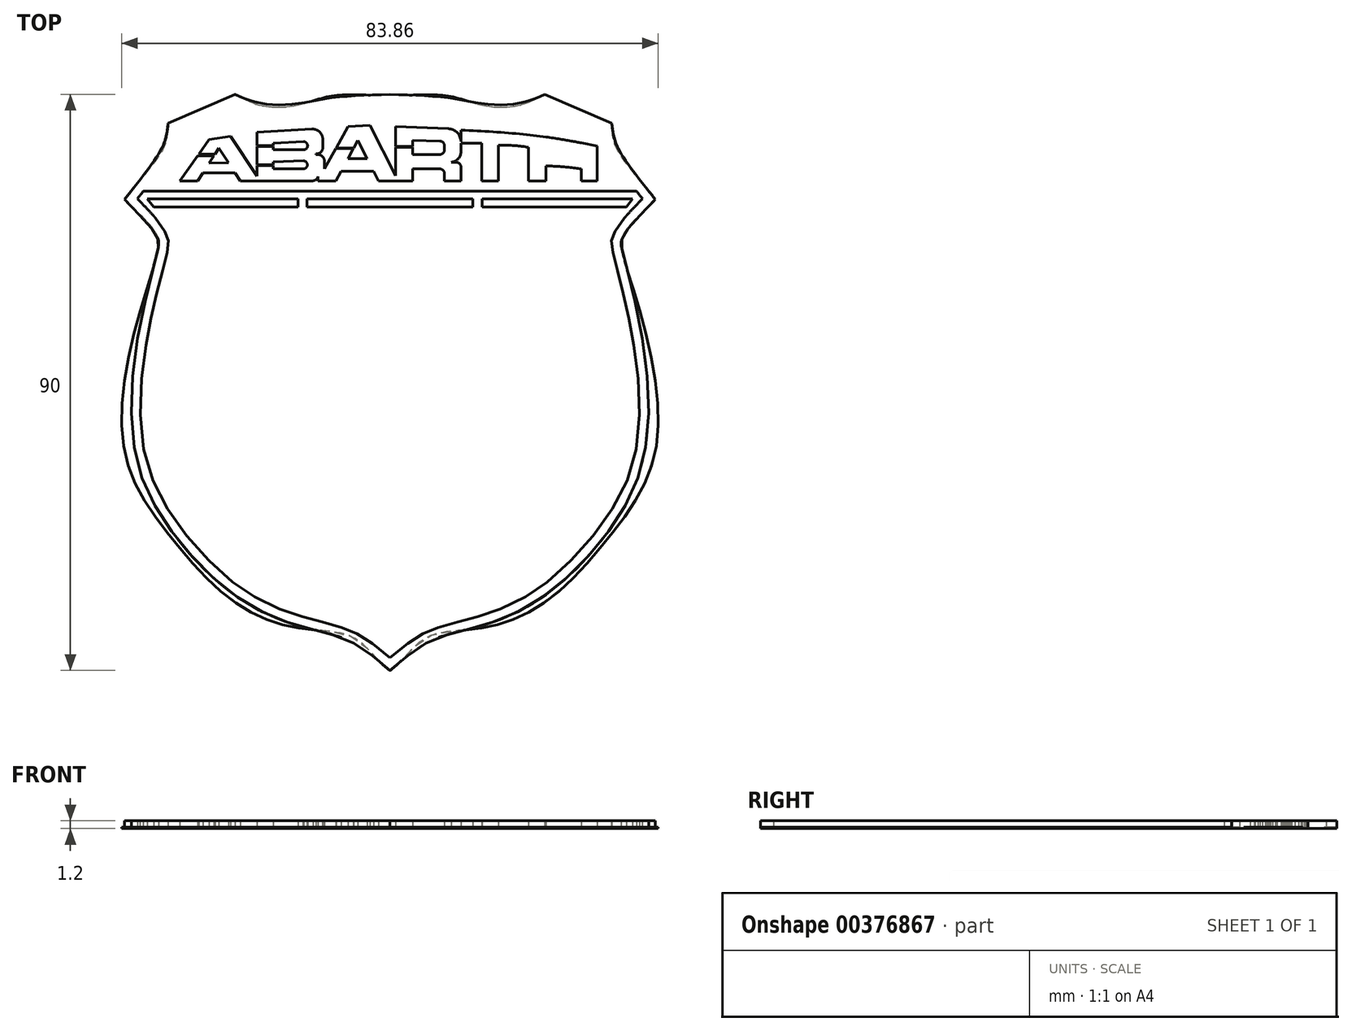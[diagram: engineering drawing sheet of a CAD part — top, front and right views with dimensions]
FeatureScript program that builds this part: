
annotation { "Feature Type Name" : "Feature", "Feature Type Description" : "" }
export const myFeature = defineFeature(function(context is Context, id is Id, definition is map)
    precondition{}
    {
        {
            var Q0;
            Q0=qCreatedBy(makeId("Top.planeOp"),FACE);
            var sketch = newSketch(context, id + "F0", { "sketchPlane" : qUnion([Q0])});
            skFitSpline(sketch, "E0", {"points": [v(-41.47, 27.67) * mm, v(-37.34, 23.25) * mm, v(-36.2, 21.38) * mm, v(-36.2, 20.2) * mm, v(-39.18, 7.45) * mm, v(-39.76, -12.14) * mm, v(-33.8, -24.6) * mm, v(-23.5, -34.67) * mm, v(-13.75, -39.08) * mm, v(-6.19, -41.36) * mm, v(0, -45.92) * mm], "startDerivative": vector(56.35, -56.79) * mm, "endDerivative": vector(62.68, -55.45) * mm});
            skFitSpline(sketch, "E1", {"points": [v(-41.47, 27.67) * mm, v(-36.79, 33.8) * mm, v(-35.15, 36.9) * mm, v(-34.66, 39.57) * mm], "startDerivative": vector(11.93, 14.97) * mm, "endDerivative": vector(1.2, 10.34) * mm});
            skLineSegment(sketch, "E2", {"start": v(-34.66, 39.57) * mm, "end": v(-24.2, 44.08) * mm});
            skFitSpline(sketch, "E3", {"points": [v(-24.2, 44.08) * mm, v(-20.64, 42.8) * mm, v(-15.26, 42.56) * mm, v(-9.28, 43.52) * mm, v(0, 44.08) * mm], "startDerivative": vector(16.73, -7.4) * mm, "endDerivative": vector(31.53, 0.89) * mm});
            skFitSpline(sketch, "E4.0", {"points": [v(-40.4, 28.73) * mm, v(-39.82, 28.14) * mm, v(-38.93, 27.25) * mm, v(-37.83, 26.1) * mm, v(-37.06, 25.25) * mm, v(-36.37, 24.45) * mm, v(-35.77, 23.67) * mm, v(-35.37, 23.07) * mm, v(-35.1, 22.6) * mm, v(-34.93, 22.26) * mm, v(-34.81, 21.96) * mm, v(-34.74, 21.72) * mm, v(-34.66, 21.45) * mm, v(-34.61, 21.08) * mm, v(-34.62, 20.65) * mm, v(-34.66, 20.25) * mm, v(-34.74, 19.86) * mm, v(-34.83, 19.41) * mm, v(-35, 18.73) * mm, v(-35.25, 17.72) * mm, v(-35.62, 16.26) * mm, v(-36.04, 14.6) * mm, v(-36.5, 12.79) * mm, v(-36.95, 10.84) * mm, v(-37.39, 8.81) * mm, v(-37.8, 6.74) * mm, v(-38.26, 3.96) * mm, v(-38.7, 0.48) * mm, v(-38.96, -3.62) * mm, v(-38.9, -7.54) * mm, v(-38.49, -11.2) * mm, v(-37.69, -14.47) * mm, v(-36.5, -17.48) * mm, v(-34.99, -20.3) * mm, v(-33.15, -23.03) * mm, v(-31.03, -25.73) * mm, v(-28.7, -28.33) * mm, v(-26.22, -30.71) * mm, v(-24.07, -32.46) * mm, v(-22.34, -33.66) * mm, v(-20.6, -34.74) * mm, v(-18.4, -35.86) * mm, v(-16.2, -36.74) * mm, v(-14.45, -37.31) * mm, v(-13.16, -37.69) * mm, v(-11.88, -38.02) * mm, v(-10.6, -38.34) * mm, v(-9.3, -38.66) * mm, v(-8.03, -39.03) * mm, v(-6.97, -39.4) * mm, v(-6.12, -39.73) * mm, v(-5.5, -40.02) * mm, v(-4.88, -40.34) * mm, v(-4.09, -40.79) * mm, v(-3.14, -41.4) * mm, v(-2.05, -42.21) * mm, v(-0.65, -43.34) * mm, v(0.34, -44.22) * mm, v(1, -44.8) * mm]});
            skFitSpline(sketch, "E5.0", {"points": [v(-40.3, 26.74) * mm, v(-39.8, 27.36) * mm, v(-38.8, 28.61) * mm, v(-37.38, 30.44) * mm, v(-36.31, 31.86) * mm, v(-35.57, 32.92) * mm, v(-34.9, 33.92) * mm, v(-34.35, 34.87) * mm, v(-33.97, 35.72) * mm, v(-33.79, 36.21) * mm, v(-33.63, 36.71) * mm, v(-33.47, 37.33) * mm, v(-33.3, 38.29) * mm, v(-33.22, 38.97) * mm, v(-33.17, 39.4) * mm]});
            skLineSegment(sketch, "E6", {"start": v(-38.54, 28.95) * mm, "end": v(0, 28.95) * mm});
            skLineSegment(sketch, "E7", {"start": v(-37.07, 25.26) * mm, "end": v(0, 25.26) * mm});
            skLineSegment(sketch, "E8", {"start": v(-37.9, 27.74) * mm, "end": v(-14.38, 27.74) * mm});
            skLineSegment(sketch, "E9", {"start": v(-36.92, 26.5) * mm, "end": v(-14.38, 26.5) * mm});
            skLineSegment(sketch, "E10", {"start": v(-14.38, 27.74) * mm, "end": v(-14.38, 26.5) * mm});
            skLineSegment(sketch, "E11", {"start": v(-37.9, 27.74) * mm, "end": v(-36.92, 26.5) * mm});
            skLineSegment(sketch, "E12", {"start": v(-12.98, 27.74) * mm, "end": v(0, 27.74) * mm});
            skLineSegment(sketch, "E13", {"start": v(-12.98, 26.5) * mm, "end": v(0, 26.5) * mm});
            skLineSegment(sketch, "E14", {"start": v(-12.98, 27.74) * mm, "end": v(-12.98, 26.5) * mm});
            skPoint(sketch, "E15.orphan", {"position": v(-13.21, 26.5) * mm});
            skLineSegment(sketch, "E16", {"start": v(-36.64, 24.77) * mm, "end": v(0, 24.77) * mm});
            skFitSpline(sketch, "E17.trimOffspring", {"points": [v(-40.4, 28.73) * mm, v(-39.82, 28.14) * mm, v(-38.93, 27.25) * mm, v(-37.83, 26.1) * mm, v(-37.06, 25.25) * mm, v(-36.37, 24.45) * mm, v(-35.77, 23.67) * mm, v(-35.37, 23.07) * mm, v(-35.1, 22.6) * mm, v(-34.93, 22.26) * mm, v(-34.81, 21.96) * mm, v(-34.74, 21.72) * mm, v(-34.66, 21.45) * mm, v(-34.61, 21.08) * mm, v(-34.62, 20.65) * mm, v(-34.66, 20.25) * mm, v(-34.74, 19.86) * mm, v(-34.83, 19.41) * mm, v(-35, 18.73) * mm, v(-35.25, 17.72) * mm, v(-35.62, 16.26) * mm, v(-36.04, 14.6) * mm, v(-36.5, 12.79) * mm, v(-36.95, 10.84) * mm, v(-37.39, 8.81) * mm, v(-37.8, 6.74) * mm, v(-38.26, 3.96) * mm, v(-38.7, 0.48) * mm, v(-38.96, -3.62) * mm, v(-38.9, -7.54) * mm, v(-38.49, -11.2) * mm, v(-37.69, -14.47) * mm, v(-36.5, -17.48) * mm, v(-34.99, -20.3) * mm, v(-33.15, -23.03) * mm, v(-31.03, -25.73) * mm, v(-28.7, -28.33) * mm, v(-26.22, -30.71) * mm, v(-24.07, -32.46) * mm, v(-22.34, -33.66) * mm, v(-20.6, -34.74) * mm, v(-18.4, -35.86) * mm, v(-16.2, -36.74) * mm, v(-14.45, -37.31) * mm, v(-13.16, -37.69) * mm, v(-11.88, -38.02) * mm, v(-10.6, -38.34) * mm, v(-9.3, -38.66) * mm, v(-8.03, -39.03) * mm, v(-6.97, -39.4) * mm, v(-6.12, -39.73) * mm, v(-5.5, -40.02) * mm, v(-4.88, -40.34) * mm, v(-4.09, -40.79) * mm, v(-3.14, -41.4) * mm, v(-2.05, -42.21) * mm, v(-0.65, -43.34) * mm, v(0.34, -44.22) * mm, v(1, -44.8) * mm]});
            skLineSegment(sketch, "E18.MirrorCS", {"start": v(37.9, 27.74) * mm, "end": v(36.92, 26.5) * mm});
            skLineSegment(sketch, "E19.MirrorCS", {"start": v(14.38, 27.74) * mm, "end": v(14.38, 26.5) * mm});
            skLineSegment(sketch, "E20.MirrorCS", {"start": v(12.98, 27.74) * mm, "end": v(12.98, 26.5) * mm});
            skFitSpline(sketch, "E21.MirrorCS", {"points": [v(41.47, 27.67) * mm, v(36.79, 33.8) * mm, v(35.15, 36.9) * mm, v(34.66, 39.57) * mm], "startDerivative": vector(-11.93, 14.97) * mm, "endDerivative": vector(-1.2, 10.34) * mm});
            skLineSegment(sketch, "E22.MirrorCS", {"start": v(12.98, 26.5) * mm, "end": v(0, 26.5) * mm});
            skLineSegment(sketch, "E23.MirrorCS", {"start": v(37.9, 27.74) * mm, "end": v(14.38, 27.74) * mm});
            skLineSegment(sketch, "E24.MirrorCS", {"start": v(34.66, 39.57) * mm, "end": v(24.2, 44.08) * mm});
            skLineSegment(sketch, "E25.MirrorCS", {"start": v(37.07, 25.26) * mm, "end": v(0, 25.26) * mm});
            skFitSpline(sketch, "E26.MirrorCS", {"points": [v(24.2, 44.08) * mm, v(20.64, 42.8) * mm, v(15.26, 42.56) * mm, v(9.28, 43.52) * mm, v(0, 44.08) * mm], "startDerivative": vector(-16.73, -7.4) * mm, "endDerivative": vector(-31.53, 0.89) * mm});
            skLineSegment(sketch, "E27.MirrorCS", {"start": v(12.98, 27.74) * mm, "end": v(0, 27.74) * mm});
            skLineSegment(sketch, "E28.MirrorCS", {"start": v(36.64, 24.77) * mm, "end": v(0, 24.77) * mm});
            skLineSegment(sketch, "E29.MirrorCS", {"start": v(36.92, 26.5) * mm, "end": v(14.38, 26.5) * mm});
            skPoint(sketch, "E30.MirrorP", {"position": v(13.21, 26.5) * mm});
            skLineSegment(sketch, "E31.MirrorCS", {"start": v(38.54, 28.95) * mm, "end": v(0, 28.95) * mm});
            skFitSpline(sketch, "E32.MirrorCS", {"points": [v(41.47, 27.67) * mm, v(37.34, 23.25) * mm, v(36.2, 21.38) * mm, v(36.2, 20.2) * mm, v(39.18, 7.45) * mm, v(39.76, -12.14) * mm, v(33.8, -24.6) * mm, v(23.5, -34.67) * mm, v(13.75, -39.08) * mm, v(6.19, -41.36) * mm, v(0, -45.92) * mm], "startDerivative": vector(-56.35, -56.79) * mm, "endDerivative": vector(-62.68, -55.45) * mm});
            skLineSegment(sketch, "E33", {"start": v(-32.83, 30.58) * mm, "end": v(-30.04, 34.53) * mm});
            skLineSegment(sketch, "E34", {"start": v(-28.26, 37.05) * mm, "end": v(-24.93, 37.53) * mm});
            skLineSegment(sketch, "E35", {"start": v(-24.93, 37.53) * mm, "end": v(-20.8, 31.35) * mm});
            skLineSegment(sketch, "E36", {"start": v(-20.8, 31.35) * mm, "end": v(-20.8, 32.99) * mm});
            skLineSegment(sketch, "E37", {"start": v(-20.8, 38.16) * mm, "end": v(-12.23, 38.67) * mm});
            skLineSegment(sketch, "E38", {"start": v(-32.83, 30.58) * mm, "end": v(-30.05, 30.58) * mm});
            skLineSegment(sketch, "E39", {"start": v(-30.05, 30.58) * mm, "end": v(-29.25, 31.8) * mm});
            skLineSegment(sketch, "E40", {"start": v(-26.72, 35.7) * mm, "end": v(-25.24, 33.42) * mm});
            skLineSegment(sketch, "E41", {"start": v(-29.25, 31.8) * mm, "end": v(-24.2, 31.8) * mm});
            skLineSegment(sketch, "E42", {"start": v(-25.24, 33.42) * mm, "end": v(-28.24, 33.35) * mm});
            skLineSegment(sketch, "E43.trimOffspring", {"start": v(-28.24, 33.35) * mm, "end": v(-27.48, 34.53) * mm});
            skLineSegment(sketch, "E44.trimOffspring", {"start": v(-24.2, 31.8) * mm, "end": v(-23.4, 30.58) * mm});
            skLineSegment(sketch, "E45.trimOffspring", {"start": v(-23.4, 30.58) * mm, "end": v(-11.99, 30.58) * mm});
            skLineSegment(sketch, "E46", {"start": v(-6.54, 39.04) * mm, "end": v(-3.12, 39.25) * mm});
            skLineSegment(sketch, "E47", {"start": v(-3.12, 39.25) * mm, "end": v(0.88, 31.36) * mm});
            skLineSegment(sketch, "E48", {"start": v(0.88, 31.36) * mm, "end": v(0.88, 35.83) * mm});
            skLineSegment(sketch, "E49", {"start": v(0.88, 39.04) * mm, "end": v(9.14, 38.73) * mm});
            skLineSegment(sketch, "E50", {"start": v(11.09, 36.44) * mm, "end": v(14.35, 36.44) * mm});
            skLineSegment(sketch, "E51", {"start": v(14.35, 36.44) * mm, "end": v(14.35, 30.58) * mm});
            skLineSegment(sketch, "E52", {"start": v(16.96, 36.17) * mm, "end": v(16.96, 30.58) * mm});
            skLineSegment(sketch, "E53", {"start": v(3.52, 36.9) * mm, "end": v(3.52, 35.93) * mm});
            skLineSegment(sketch, "E54", {"start": v(8.52, 36.06) * mm, "end": v(8.52, 35.45) * mm});
            skLineSegment(sketch, "E55", {"start": v(3.52, 36.9) * mm, "end": v(7.78, 36.81) * mm});
            skLineSegment(sketch, "E56", {"start": v(3.52, 34.7) * mm, "end": v(7.77, 34.7) * mm});
            skPoint(sketch, "E57.orphan", {"position": v(8.52, 36.97) * mm});
            skLineSegment(sketch, "E58", {"start": v(3.52, 32.45) * mm, "end": v(7.77, 32.45) * mm});
            skLineSegment(sketch, "E59", {"start": v(8.52, 31.7) * mm, "end": v(8.52, 30.58) * mm});
            skLineSegment(sketch, "E60", {"start": v(11.09, 32.75) * mm, "end": v(11.09, 30.58) * mm});
            skLineSegment(sketch, "E61", {"start": v(11.09, 36.7) * mm, "end": v(11.09, 38.49) * mm});
            skLineSegment(sketch, "E62", {"start": v(9.6, 33.5) * mm, "end": v(10.34, 33.5) * mm});
            skLineSegment(sketch, "E63.trimOffspring", {"start": v(3.52, 32.45) * mm, "end": v(3.52, 30.58) * mm});
            skPoint(sketch, "E64.visualSharp", {"position": v(8.52, 36.8) * mm});
            skArc(sketch, "E64.filletArc", {"start": v(8.52, 36.06) * mm, "mid": v(8.3, 36.59) * mm, "end": v(7.78, 36.81) * mm});
            skPoint(sketch, "E65.visualSharp", {"position": v(8.52, 34.7) * mm});
            skArc(sketch, "E65.filletArc", {"start": v(7.77, 34.7) * mm, "mid": v(8.3, 34.91) * mm, "end": v(8.52, 35.45) * mm});
            skArc(sketch, "E66.filletArc", {"start": v(8.52, 31.7) * mm, "mid": v(8.3, 32.23) * mm, "end": v(7.77, 32.45) * mm});
            skPoint(sketch, "E67.visualSharp", {"position": v(11.09, 33.5) * mm});
            skArc(sketch, "E67.filletArc", {"start": v(11.09, 32.75) * mm, "mid": v(10.87, 33.28) * mm, "end": v(10.34, 33.5) * mm});
            skLineSegment(sketch, "E68", {"start": v(-8.43, 30.58) * mm, "end": v(-7.62, 32.1) * mm});
            skLineSegment(sketch, "E69", {"start": v(-5.03, 36.94) * mm, "end": v(-3.54, 34.04) * mm});
            skLineSegment(sketch, "E70", {"start": v(-7.62, 32.1) * mm, "end": v(-2.54, 32.1) * mm});
            skLineSegment(sketch, "E71", {"start": v(-6.58, 34.04) * mm, "end": v(-3.54, 34.04) * mm});
            skLineSegment(sketch, "E72.trimOffspring", {"start": v(-6.58, 34.04) * mm, "end": v(-5.73, 35.62) * mm});
            skLineSegment(sketch, "E73.trimOffspring", {"start": v(-2.54, 32.1) * mm, "end": v(-1.76, 30.58) * mm});
            skLineSegment(sketch, "E74.trimOffspring", {"start": v(-1.76, 30.58) * mm, "end": v(3.52, 30.58) * mm});
            skLineSegment(sketch, "E75.trimOffspring", {"start": v(8.52, 30.58) * mm, "end": v(11.09, 30.58) * mm});
            skLineSegment(sketch, "E76", {"start": v(21.66, 35.8) * mm, "end": v(21.66, 30.58) * mm});
            skLineSegment(sketch, "E77", {"start": v(24.37, 32.92) * mm, "end": v(24.37, 30.58) * mm});
            skLineSegment(sketch, "E78", {"start": v(29.9, 32.46) * mm, "end": v(29.9, 30.58) * mm});
            skLineSegment(sketch, "E79", {"start": v(24.37, 34.71) * mm, "end": v(24.37, 37.44) * mm});
            skLineSegment(sketch, "E80", {"start": v(29.9, 34.15) * mm, "end": v(29.9, 36.5) * mm});
            skFitSpline(sketch, "E81", {"points": [v(24.37, 34.71) * mm, v(27.2, 34.5) * mm, v(29.9, 34.15) * mm], "startDerivative": vector(5.62, -0.36) * mm, "endDerivative": vector(5.44, -0.76) * mm});
            skFitSpline(sketch, "E82", {"points": [v(24.37, 32.92) * mm, v(27.07, 32.78) * mm, v(29.9, 32.46) * mm], "startDerivative": vector(5.44, -0.19) * mm, "endDerivative": vector(5.62, -0.73) * mm});
            skLineSegment(sketch, "E83", {"start": v(32.4, 36.02) * mm, "end": v(32.4, 30.58) * mm});
            skFitSpline(sketch, "E84", {"points": [v(32.4, 36.02) * mm, v(29.9, 36.5) * mm, v(24.37, 37.44) * mm, v(11.09, 38.49) * mm], "startDerivative": vector(-11.08, 2.13) * mm, "endDerivative": vector(-30.4, 0.87) * mm});
            skFitSpline(sketch, "E85", {"points": [v(16.96, 36.17) * mm, v(19.52, 36.08) * mm, v(21.66, 35.8) * mm], "startDerivative": vector(5.24, 0.1) * mm, "endDerivative": vector(6.05, -1.14) * mm});
            skLineSegment(sketch, "E86.trimOffspring", {"start": v(29.9, 30.58) * mm, "end": v(32.4, 30.58) * mm});
            skLineSegment(sketch, "E87.trimOffspring", {"start": v(21.66, 30.58) * mm, "end": v(24.37, 30.58) * mm});
            skLineSegment(sketch, "E88.trimOffspring", {"start": v(14.35, 30.58) * mm, "end": v(16.96, 30.58) * mm});
            skLineSegment(sketch, "E89", {"start": v(-18.2, 36.49) * mm, "end": v(-18.2, 36.06) * mm});
            skLineSegment(sketch, "E90", {"start": v(-18.2, 32.46) * mm, "end": v(-13.58, 32.46) * mm});
            skLineSegment(sketch, "E91", {"start": v(-18.2, 33.52) * mm, "end": v(-13.5, 33.72) * mm});
            skLineSegment(sketch, "E92", {"start": v(-18.2, 35.43) * mm, "end": v(-13.54, 35.43) * mm});
            skLineSegment(sketch, "E93", {"start": v(-18.2, 36.49) * mm, "end": v(-13.47, 36.7) * mm});
            skLineSegment(sketch, "E94", {"start": v(-13.47, 36.7) * mm, "end": v(-13.54, 35.43) * mm, "construction": true});
            skLineSegment(sketch, "E95", {"start": v(-13.5, 33.72) * mm, "end": v(-13.58, 32.46) * mm, "construction": true});
            skLineSegment(sketch, "E96.trimOffspring", {"start": v(-18.2, 33.52) * mm, "end": v(-18.2, 33.09) * mm});
            skArc(sketch, "E97", {"start": v(-13.54, 35.43) * mm, "mid": v(-12.86, 36.1) * mm, "end": v(-13.6, 36.7) * mm});
            skArc(sketch, "E98", {"start": v(-13.58, 32.46) * mm, "mid": v(-12.9, 33.11) * mm, "end": v(-13.63, 33.71) * mm});
            skLineSegment(sketch, "E99", {"start": v(-10.5, 37.04) * mm, "end": v(-10.5, 35.92) * mm});
            skLineSegment(sketch, "E100", {"start": v(-10.26, 33.76) * mm, "end": v(-10.26, 32.46) * mm});
            skLineSegment(sketch, "E101.trimOffspring", {"start": v(-11.25, 30.58) * mm, "end": v(-8.43, 30.58) * mm});
            skLineSegment(sketch, "E102.trimOffspring", {"start": v(-10.26, 32.46) * mm, "end": v(-8.47, 35.62) * mm});
            skLineSegment(sketch, "E103", {"start": v(-11.25, 31.24) * mm, "end": v(-11.25, 30.58) * mm});
            skFitSpline(sketch, "E104", {"points": [v(-11.99, 30.58) * mm, v(-11.5, 30.8) * mm, v(-11.25, 31.24) * mm], "startDerivative": vector(1.07, 0.32) * mm, "endDerivative": vector(0.41, 0.99) * mm});
            skLineSegment(sketch, "E105", {"start": v(-11.54, 34.66) * mm, "end": v(-11.16, 34.66) * mm});
            skArc(sketch, "E106.filletArc", {"start": v(-10.26, 33.76) * mm, "mid": v(-10.52, 34.4) * mm, "end": v(-11.16, 34.66) * mm});
            skLineSegment(sketch, "E107", {"start": v(-11.54, 34.66) * mm, "end": v(-11.54, 34.79) * mm});
            skFitSpline(sketch, "E108", {"points": [v(-11.54, 34.79) * mm, v(-10.9, 34.98) * mm, v(-10.51, 35.57) * mm, v(-10.5, 35.92) * mm], "startDerivative": vector(1.88, 0.23) * mm, "endDerivative": vector(0.1, 1.77) * mm});
            skArc(sketch, "E109", {"start": v(-10.5, 37.04) * mm, "mid": v(-11, 38.23) * mm, "end": v(-12.23, 38.67) * mm});
            skPoint(sketch, "E109.first.point", {"position": v(-12.23, 38.67) * mm});
            skPoint(sketch, "E109.second.point", {"position": v(-10.5, 37.04) * mm});
            skPoint(sketch, "E109.third.point", {"position": v(-13.76, 37.07) * mm});
            skPoint(sketch, "E110.second.point", {"position": v(11.09, 36.7) * mm});
            skPoint(sketch, "E110.third.point", {"position": v(7.3, 35.72) * mm});
            skArc(sketch, "E111.trimOffspring", {"start": v(11.09, 36.7) * mm, "mid": v(10.52, 38.1) * mm, "end": v(9.14, 38.73) * mm});
            skLineSegment(sketch, "E112", {"start": v(11.09, 36.44) * mm, "end": v(11.09, 35.12) * mm});
            skPoint(sketch, "E113.second.point", {"position": v(11.09, 35.12) * mm});
            skPoint(sketch, "E113.third.point", {"position": v(10.14, 36.6) * mm});
            skArc(sketch, "E114.trimOffspring", {"start": v(9.6, 33.5) * mm, "mid": v(10.66, 34.02) * mm, "end": v(11.09, 35.12) * mm});
            skLineSegment(sketch, "E115", {"start": v(-35.21, -19.82) * mm, "end": v(-22.8, -14.18) * mm});
            skLineSegment(sketch, "E116", {"start": v(-34.28, -21.33) * mm, "end": v(-5.34, -8.17) * mm});
            skFitSpline(sketch, "E117.0", {"points": [v(40.4, 28.73) * mm, v(39.82, 28.14) * mm, v(38.93, 27.25) * mm, v(37.83, 26.1) * mm, v(37.06, 25.25) * mm, v(36.37, 24.45) * mm, v(35.77, 23.67) * mm, v(35.37, 23.07) * mm, v(35.1, 22.6) * mm, v(34.93, 22.26) * mm, v(34.81, 21.96) * mm, v(34.74, 21.72) * mm, v(34.66, 21.45) * mm, v(34.61, 21.08) * mm, v(34.62, 20.65) * mm, v(34.66, 20.25) * mm, v(34.74, 19.86) * mm, v(34.83, 19.41) * mm, v(35, 18.73) * mm, v(35.25, 17.72) * mm, v(35.62, 16.26) * mm, v(36.04, 14.6) * mm, v(36.5, 12.79) * mm, v(36.95, 10.84) * mm, v(37.39, 8.81) * mm, v(37.8, 6.74) * mm, v(38.26, 3.96) * mm, v(38.7, 0.48) * mm, v(38.96, -3.62) * mm, v(38.9, -7.54) * mm, v(38.49, -11.2) * mm, v(37.69, -14.47) * mm, v(36.5, -17.48) * mm, v(34.99, -20.3) * mm, v(33.15, -23.03) * mm, v(31.03, -25.73) * mm, v(28.7, -28.33) * mm, v(26.22, -30.71) * mm, v(24.07, -32.46) * mm, v(22.34, -33.66) * mm, v(20.6, -34.74) * mm, v(18.4, -35.86) * mm, v(16.2, -36.74) * mm, v(14.45, -37.31) * mm, v(13.16, -37.69) * mm, v(11.88, -38.02) * mm, v(10.6, -38.34) * mm, v(9.3, -38.66) * mm, v(8.03, -39.03) * mm, v(6.97, -39.4) * mm, v(6.12, -39.73) * mm, v(5.5, -40.02) * mm, v(4.88, -40.34) * mm, v(4.09, -40.79) * mm, v(3.14, -41.4) * mm, v(2.05, -42.21) * mm, v(0.65, -43.34) * mm, v(-0.34, -44.22) * mm, v(-1, -44.8) * mm]});
            skFitSpline(sketch, "E118.0", {"points": [v(40.3, 26.74) * mm, v(39.8, 27.36) * mm, v(38.8, 28.61) * mm, v(37.38, 30.44) * mm, v(36.31, 31.86) * mm, v(35.57, 32.92) * mm, v(34.9, 33.92) * mm, v(34.35, 34.87) * mm, v(33.97, 35.72) * mm, v(33.79, 36.21) * mm, v(33.63, 36.71) * mm, v(33.47, 37.33) * mm, v(33.3, 38.29) * mm, v(33.22, 38.97) * mm, v(33.17, 39.4) * mm]});
            skFitSpline(sketch, "E119.trimOffspring", {"points": [v(40.4, 28.73) * mm, v(39.82, 28.14) * mm, v(38.93, 27.25) * mm, v(37.83, 26.1) * mm, v(37.06, 25.25) * mm, v(36.37, 24.45) * mm, v(35.77, 23.67) * mm, v(35.37, 23.07) * mm, v(35.1, 22.6) * mm, v(34.93, 22.26) * mm, v(34.81, 21.96) * mm, v(34.74, 21.72) * mm, v(34.66, 21.45) * mm, v(34.61, 21.08) * mm, v(34.62, 20.65) * mm, v(34.66, 20.25) * mm, v(34.74, 19.86) * mm, v(34.83, 19.41) * mm, v(35, 18.73) * mm, v(35.25, 17.72) * mm, v(35.62, 16.26) * mm, v(36.04, 14.6) * mm, v(36.5, 12.79) * mm, v(36.95, 10.84) * mm, v(37.39, 8.81) * mm, v(37.8, 6.74) * mm, v(38.26, 3.96) * mm, v(38.7, 0.48) * mm, v(38.96, -3.62) * mm, v(38.9, -7.54) * mm, v(38.49, -11.2) * mm, v(37.69, -14.47) * mm, v(36.5, -17.48) * mm, v(34.99, -20.3) * mm, v(33.15, -23.03) * mm, v(31.03, -25.73) * mm, v(28.7, -28.33) * mm, v(26.22, -30.71) * mm, v(24.07, -32.46) * mm, v(22.34, -33.66) * mm, v(20.6, -34.74) * mm, v(18.4, -35.86) * mm, v(16.2, -36.74) * mm, v(14.45, -37.31) * mm, v(13.16, -37.69) * mm, v(11.88, -38.02) * mm, v(10.6, -38.34) * mm, v(9.3, -38.66) * mm, v(8.03, -39.03) * mm, v(6.97, -39.4) * mm, v(6.12, -39.73) * mm, v(5.5, -40.02) * mm, v(4.88, -40.34) * mm, v(4.09, -40.79) * mm, v(3.14, -41.4) * mm, v(2.05, -42.21) * mm, v(0.65, -43.34) * mm, v(-0.34, -44.22) * mm, v(-1, -44.8) * mm]});
            skFitSpline(sketch, "E120.trimOffspring", {"points": [v(40.4, 28.73) * mm, v(39.82, 28.14) * mm, v(38.93, 27.25) * mm, v(37.83, 26.1) * mm, v(37.06, 25.25) * mm, v(36.37, 24.45) * mm, v(35.77, 23.67) * mm, v(35.37, 23.07) * mm, v(35.1, 22.6) * mm, v(34.93, 22.26) * mm, v(34.81, 21.96) * mm, v(34.74, 21.72) * mm, v(34.66, 21.45) * mm, v(34.61, 21.08) * mm, v(34.62, 20.65) * mm, v(34.66, 20.25) * mm, v(34.74, 19.86) * mm, v(34.83, 19.41) * mm, v(35, 18.73) * mm, v(35.25, 17.72) * mm, v(35.62, 16.26) * mm, v(36.04, 14.6) * mm, v(36.5, 12.79) * mm, v(36.95, 10.84) * mm, v(37.39, 8.81) * mm, v(37.8, 6.74) * mm, v(38.26, 3.96) * mm, v(38.7, 0.48) * mm, v(38.96, -3.62) * mm, v(38.9, -7.54) * mm, v(38.49, -11.2) * mm, v(37.69, -14.47) * mm, v(36.5, -17.48) * mm, v(34.99, -20.3) * mm, v(33.15, -23.03) * mm, v(31.03, -25.73) * mm, v(28.7, -28.33) * mm, v(26.22, -30.71) * mm, v(24.07, -32.46) * mm, v(22.34, -33.66) * mm, v(20.6, -34.74) * mm, v(18.4, -35.86) * mm, v(16.2, -36.74) * mm, v(14.45, -37.31) * mm, v(13.16, -37.69) * mm, v(11.88, -38.02) * mm, v(10.6, -38.34) * mm, v(9.3, -38.66) * mm, v(8.03, -39.03) * mm, v(6.97, -39.4) * mm, v(6.12, -39.73) * mm, v(5.5, -40.02) * mm, v(4.88, -40.34) * mm, v(4.09, -40.79) * mm, v(3.14, -41.4) * mm, v(2.05, -42.21) * mm, v(0.65, -43.34) * mm, v(-0.34, -44.22) * mm, v(-1, -44.8) * mm]});
            skFitSpline(sketch, "E121.trimOffspring", {"points": [v(-40.4, 28.73) * mm, v(-39.82, 28.14) * mm, v(-38.93, 27.25) * mm, v(-37.83, 26.1) * mm, v(-37.06, 25.25) * mm, v(-36.37, 24.45) * mm, v(-35.77, 23.67) * mm, v(-35.37, 23.07) * mm, v(-35.1, 22.6) * mm, v(-34.93, 22.26) * mm, v(-34.81, 21.96) * mm, v(-34.74, 21.72) * mm, v(-34.66, 21.45) * mm, v(-34.61, 21.08) * mm, v(-34.62, 20.65) * mm, v(-34.66, 20.25) * mm, v(-34.74, 19.86) * mm, v(-34.83, 19.41) * mm, v(-35, 18.73) * mm, v(-35.25, 17.72) * mm, v(-35.62, 16.26) * mm, v(-36.04, 14.6) * mm, v(-36.5, 12.79) * mm, v(-36.95, 10.84) * mm, v(-37.39, 8.81) * mm, v(-37.8, 6.74) * mm, v(-38.26, 3.96) * mm, v(-38.7, 0.48) * mm, v(-38.96, -3.62) * mm, v(-38.9, -7.54) * mm, v(-38.49, -11.2) * mm, v(-37.69, -14.47) * mm, v(-36.5, -17.48) * mm, v(-34.99, -20.3) * mm, v(-33.15, -23.03) * mm, v(-31.03, -25.73) * mm, v(-28.7, -28.33) * mm, v(-26.22, -30.71) * mm, v(-24.07, -32.46) * mm, v(-22.34, -33.66) * mm, v(-20.6, -34.74) * mm, v(-18.4, -35.86) * mm, v(-16.2, -36.74) * mm, v(-14.45, -37.31) * mm, v(-13.16, -37.69) * mm, v(-11.88, -38.02) * mm, v(-10.6, -38.34) * mm, v(-9.3, -38.66) * mm, v(-8.03, -39.03) * mm, v(-6.97, -39.4) * mm, v(-6.12, -39.73) * mm, v(-5.5, -40.02) * mm, v(-4.88, -40.34) * mm, v(-4.09, -40.79) * mm, v(-3.14, -41.4) * mm, v(-2.05, -42.21) * mm, v(-0.65, -43.34) * mm, v(0.34, -44.22) * mm, v(1, -44.8) * mm]});
            skLineSegment(sketch, "E122", {"start": v(-11.89, 16.4) * mm, "end": v(-25.26, 3.77) * mm});
            skLineSegment(sketch, "E123", {"start": v(-25.33, 3.55) * mm, "end": v(-22.8, -14.18) * mm});
            skLineSegment(sketch, "E124", {"start": v(-3.25, -5.28) * mm, "end": v(-6.47, -0.83) * mm});
            skLineSegment(sketch, "E125", {"start": v(-6.47, -0.83) * mm, "end": v(-18.46, -9.04) * mm});
            skLineSegment(sketch, "E126", {"start": v(-18.46, -9.04) * mm, "end": v(-20.67, -4.75) * mm});
            skLineSegment(sketch, "E127", {"start": v(-20.5, -4.39) * mm, "end": v(-15.42, -3.58) * mm});
            skLineSegment(sketch, "E128", {"start": v(-15.42, -3.58) * mm, "end": v(-8.97, 6.38) * mm});
            skLineSegment(sketch, "E129", {"start": v(-9.3, 6.74) * mm, "end": v(-14.59, 4.03) * mm});
            skLineSegment(sketch, "E130", {"start": v(-14.94, 4.32) * mm, "end": v(-11.48, 16.15) * mm});
            skArc(sketch, "E131.filletArc", {"start": v(-11.48, 16.15) * mm, "mid": v(-11.58, 16.43) * mm, "end": v(-11.89, 16.4) * mm});
            skPoint(sketch, "E132.visualSharp", {"position": v(-15.1, 3.76) * mm});
            skArc(sketch, "E132.filletArc", {"start": v(-14.94, 4.32) * mm, "mid": v(-14.86, 4.06) * mm, "end": v(-14.59, 4.03) * mm});
            skPoint(sketch, "E133.visualSharp", {"position": v(-8.47, 7.16) * mm});
            skArc(sketch, "E133.filletArc", {"start": v(-8.97, 6.38) * mm, "mid": v(-9, 6.68) * mm, "end": v(-9.3, 6.74) * mm});
            skPoint(sketch, "E134.visualSharp", {"position": v(-20.83, -4.44) * mm});
            skArc(sketch, "E134.filletArc", {"start": v(-20.5, -4.39) * mm, "mid": v(-20.68, -4.52) * mm, "end": v(-20.67, -4.75) * mm});
            skPoint(sketch, "E135.visualSharp", {"position": v(-25.35, 3.68) * mm});
            skArc(sketch, "E135.filletArc", {"start": v(-25.26, 3.77) * mm, "mid": v(-25.32, 3.67) * mm, "end": v(-25.33, 3.55) * mm});
            skLineSegment(sketch, "E136", {"start": v(-3.25, -5.28) * mm, "end": v(-4.18, 1.2) * mm});
            skLineSegment(sketch, "E137", {"start": v(-4.18, 1.2) * mm, "end": v(0, 1.2) * mm});
            skLineSegment(sketch, "E138", {"start": v(0, 1.2) * mm, "end": v(2.9, 4.15) * mm});
            skLineSegment(sketch, "E139", {"start": v(2.9, 4.15) * mm, "end": v(7.17, -0.55) * mm});
            skLineSegment(sketch, "E140", {"start": v(7.17, -0.55) * mm, "end": v(6.13, 5.05) * mm});
            skLineSegment(sketch, "E141", {"start": v(6.13, 5.05) * mm, "end": v(19.82, 8.7) * mm});
            skLineSegment(sketch, "E142", {"start": v(19.82, 8.7) * mm, "end": v(17.92, 12.78) * mm});
            skLineSegment(sketch, "E143", {"start": v(17.53, 12.86) * mm, "end": v(13.8, 9.6) * mm});
            skLineSegment(sketch, "E144", {"start": v(13.8, 9.6) * mm, "end": v(1.97, 11.4) * mm});
            skLineSegment(sketch, "E145", {"start": v(1.9, 11.87) * mm, "end": v(7.3, 14.27) * mm});
            skLineSegment(sketch, "E146", {"start": v(7.3, 14.72) * mm, "end": v(-3.88, 19.84) * mm});
            skLineSegment(sketch, "E147", {"start": v(-3.8, 20.31) * mm, "end": v(14.82, 22.18) * mm});
            skLineSegment(sketch, "E148", {"start": v(15.03, 22.1) * mm, "end": v(26.81, 8.39) * mm});
            skPoint(sketch, "E149.visualSharp", {"position": v(17.78, 13.08) * mm});
            skArc(sketch, "E149.filletArc", {"start": v(17.92, 12.78) * mm, "mid": v(17.74, 12.91) * mm, "end": v(17.53, 12.86) * mm});
            skPoint(sketch, "E150.visualSharp", {"position": v(1.12, 11.52) * mm});
            skArc(sketch, "E150.filletArc", {"start": v(1.9, 11.87) * mm, "mid": v(1.76, 11.6) * mm, "end": v(1.97, 11.4) * mm});
            skPoint(sketch, "E151.visualSharp", {"position": v(7.81, 14.5) * mm});
            skArc(sketch, "E151.filletArc", {"start": v(7.3, 14.27) * mm, "mid": v(7.45, 14.5) * mm, "end": v(7.3, 14.72) * mm});
            skPoint(sketch, "E152.visualSharp", {"position": v(-4.72, 20.22) * mm});
            skArc(sketch, "E152.filletArc", {"start": v(-3.8, 20.31) * mm, "mid": v(-4.02, 20.1) * mm, "end": v(-3.88, 19.84) * mm});
            skPoint(sketch, "E153.visualSharp", {"position": v(14.95, 22.2) * mm});
            skArc(sketch, "E153.filletArc", {"start": v(15.03, 22.1) * mm, "mid": v(14.94, 22.17) * mm, "end": v(14.82, 22.18) * mm});
            skLineSegment(sketch, "E154.trimOffspring", {"start": v(26.81, 8.39) * mm, "end": v(36.49, 12.79) * mm});
            skLineSegment(sketch, "E155", {"start": v(-5.04, -8.54) * mm, "end": v(-6.83, -11.04) * mm});
            skLineSegment(sketch, "E156", {"start": v(-6.83, -11.04) * mm, "end": v(-7.92, -11.04) * mm});
            skLineSegment(sketch, "E157", {"start": v(-8.06, -11.5) * mm, "end": v(-5.7, -13.12) * mm});
            skLineSegment(sketch, "E158", {"start": v(-5.7, -13.12) * mm, "end": v(-1.62, -9.19) * mm});
            skLineSegment(sketch, "E159", {"start": v(-1.62, -9.19) * mm, "end": v(-0.82, -10.02) * mm});
            skLineSegment(sketch, "E160", {"start": v(-0.82, -10.02) * mm, "end": v(-4.5, -14.02) * mm});
            skLineSegment(sketch, "E161", {"start": v(-4.5, -14.02) * mm, "end": v(-6.1, -14.24) * mm});
            skLineSegment(sketch, "E162", {"start": v(-6.1, -14.24) * mm, "end": v(-3.45, -16.22) * mm});
            skLineSegment(sketch, "E163", {"start": v(-3.45, -16.22) * mm, "end": v(0.6, -12.32) * mm});
            skLineSegment(sketch, "E164", {"start": v(0.6, -12.32) * mm, "end": v(1.38, -13.17) * mm});
            skLineSegment(sketch, "E165", {"start": v(1.38, -13.17) * mm, "end": v(-2.15, -16.97) * mm});
            skLineSegment(sketch, "E166", {"start": v(-2.15, -16.97) * mm, "end": v(-3.85, -16.97) * mm});
            skLineSegment(sketch, "E167", {"start": v(-3.85, -16.97) * mm, "end": v(-1.16, -19.2) * mm});
            skLineSegment(sketch, "E168", {"start": v(-1.16, -19.2) * mm, "end": v(2.92, -15.35) * mm});
            skLineSegment(sketch, "E169", {"start": v(2.92, -15.35) * mm, "end": v(3.64, -16.34) * mm});
            skLineSegment(sketch, "E170", {"start": v(3.64, -16.34) * mm, "end": v(0.54, -20.06) * mm});
            skLineSegment(sketch, "E171", {"start": v(0.54, -20.06) * mm, "end": v(-1.48, -20.1) * mm});
            skLineSegment(sketch, "E172", {"start": v(-1.48, -20.1) * mm, "end": v(1.4, -22.26) * mm});
            skLineSegment(sketch, "E173", {"start": v(1.4, -22.26) * mm, "end": v(5.25, -18.45) * mm});
            skLineSegment(sketch, "E174", {"start": v(5.25, -18.45) * mm, "end": v(5.53, -18.64) * mm});
            skLineSegment(sketch, "E175", {"start": v(5.53, -18.64) * mm, "end": v(5.33, -24.62) * mm});
            skLineSegment(sketch, "E176", {"start": v(5.33, -24.62) * mm, "end": v(5.01, -24.66) * mm});
            skLineSegment(sketch, "E177", {"start": v(5.01, -24.66) * mm, "end": v(1.5, -28.5) * mm});
            skLineSegment(sketch, "E178", {"start": v(1.5, -28.5) * mm, "end": v(1.5, -29.14) * mm});
            skLineSegment(sketch, "E179", {"start": v(1.5, -29.14) * mm, "end": v(-3.7, -30.63) * mm});
            skLineSegment(sketch, "E180", {"start": v(-3.7, -30.63) * mm, "end": v(-3.92, -31.01) * mm});
            skLineSegment(sketch, "E181", {"start": v(-3.92, -31.01) * mm, "end": v(-10.32, -26.75) * mm});
            skLineSegment(sketch, "E182", {"start": v(-10.32, -26.75) * mm, "end": v(-11, -26.75) * mm});
            skLineSegment(sketch, "E183", {"start": v(-11, -26.75) * mm, "end": v(-10.53, -26.45) * mm});
            skLineSegment(sketch, "E184", {"start": v(-10.53, -26.45) * mm, "end": v(-11.61, -15.5) * mm});
            skLineSegment(sketch, "E185", {"start": v(-12.1, -15.44) * mm, "end": v(-16.5, -28.57) * mm});
            skLineSegment(sketch, "E186", {"start": v(-16.17, -28.88) * mm, "end": v(-12.15, -27.22) * mm});
            skLineSegment(sketch, "E187", {"start": v(-12.15, -27.22) * mm, "end": v(-12.7, -27.94) * mm});
            skLineSegment(sketch, "E188", {"start": v(-12.7, -27.94) * mm, "end": v(-4.29, -35.37) * mm});
            skLineSegment(sketch, "E189", {"start": v(-4.29, -35.37) * mm, "end": v(-3.99, -34.83) * mm});
            skLineSegment(sketch, "E190", {"start": v(-3.99, -34.83) * mm, "end": v(-3.6, -35.22) * mm});
            skLineSegment(sketch, "E191", {"start": v(-3.6, -35.22) * mm, "end": v(4.47, -33.7) * mm});
            skLineSegment(sketch, "E192", {"start": v(4.47, -33.7) * mm, "end": v(4.37, -33.2) * mm});
            skLineSegment(sketch, "E193", {"start": v(4.37, -33.2) * mm, "end": v(4.76, -33.35) * mm});
            skLineSegment(sketch, "E194", {"start": v(4.76, -33.35) * mm, "end": v(11.78, -25.78) * mm});
            skLineSegment(sketch, "E195", {"start": v(11.88, -25.43) * mm, "end": v(11.98, -16.63) * mm});
            skLineSegment(sketch, "E196", {"start": v(11.98, -16.63) * mm, "end": v(11.54, -16.53) * mm});
            skLineSegment(sketch, "E197", {"start": v(11.54, -16.53) * mm, "end": v(12.18, -16.14) * mm});
            skLineSegment(sketch, "E198", {"start": v(12.18, -16.14) * mm, "end": v(11.93, -15.3) * mm});
            skLineSegment(sketch, "E199", {"start": v(11.93, -15.3) * mm, "end": v(17.17, -15) * mm});
            skLineSegment(sketch, "E200", {"start": v(17.17, -15) * mm, "end": v(17.47, -11.89) * mm});
            skLineSegment(sketch, "E201", {"start": v(17.47, -11.89) * mm, "end": v(16.28, -12.68) * mm});
            skLineSegment(sketch, "E202", {"start": v(16.28, -12.68) * mm, "end": v(11.24, -12.83) * mm});
            skLineSegment(sketch, "E203", {"start": v(11.24, -12.83) * mm, "end": v(10.9, -11.6) * mm});
            skLineSegment(sketch, "E204", {"start": v(10.9, -11.6) * mm, "end": v(16.68, -11.2) * mm});
            skLineSegment(sketch, "E205", {"start": v(16.68, -11.2) * mm, "end": v(16.78, -7.93) * mm});
            skLineSegment(sketch, "E206", {"start": v(16.78, -7.93) * mm, "end": v(15.4, -8.82) * mm});
            skLineSegment(sketch, "E207", {"start": v(15.4, -8.82) * mm, "end": v(10.1, -8.97) * mm});
            skLineSegment(sketch, "E208", {"start": v(10.1, -8.97) * mm, "end": v(9.78, -7.78) * mm});
            skLineSegment(sketch, "E209", {"start": v(9.78, -7.78) * mm, "end": v(15.63, -7.4) * mm});
            skLineSegment(sketch, "E210", {"start": v(15.63, -7.4) * mm, "end": v(15.95, -4.17) * mm});
            skLineSegment(sketch, "E211", {"start": v(15.95, -4.17) * mm, "end": v(14.53, -5.09) * mm});
            skLineSegment(sketch, "E212", {"start": v(14.53, -5.09) * mm, "end": v(9.1, -5.12) * mm});
            skLineSegment(sketch, "E213", {"start": v(9.1, -5.12) * mm, "end": v(8.77, -4) * mm});
            skLineSegment(sketch, "E214", {"start": v(8.77, -4) * mm, "end": v(14.74, -3.64) * mm});
            skLineSegment(sketch, "E215", {"start": v(14.74, -3.64) * mm, "end": v(15.46, -0.4) * mm});
            skLineSegment(sketch, "E216", {"start": v(15.04, -0.17) * mm, "end": v(14.06, -1.19) * mm});
            skLineSegment(sketch, "E217", {"start": v(14.06, -1.19) * mm, "end": v(11.2, -1.17) * mm});
            skPoint(sketch, "E218.visualSharp", {"position": v(15.66, 0.47) * mm});
            skArc(sketch, "E218.filletArc", {"start": v(15.46, -0.4) * mm, "mid": v(15.34, -0.13) * mm, "end": v(15.04, -0.17) * mm});
            skPoint(sketch, "E219.visualSharp", {"position": v(-8.73, -11.04) * mm});
            skArc(sketch, "E219.filletArc", {"start": v(-7.92, -11.04) * mm, "mid": v(-8.16, -11.22) * mm, "end": v(-8.06, -11.5) * mm});
            skPoint(sketch, "E220.visualSharp", {"position": v(-11.73, -14.34) * mm});
            skArc(sketch, "E220.filletArc", {"start": v(-11.61, -15.5) * mm, "mid": v(-11.83, -15.27) * mm, "end": v(-12.1, -15.44) * mm});
            skPoint(sketch, "E221.visualSharp", {"position": v(-16.67, -29.1) * mm});
            skArc(sketch, "E221.filletArc", {"start": v(-16.5, -28.57) * mm, "mid": v(-16.43, -28.83) * mm, "end": v(-16.17, -28.88) * mm});
            skLineSegment(sketch, "E222.trimOffspring", {"start": v(11.1, -0.69) * mm, "end": v(36.9, 11.04) * mm});
            skPoint(sketch, "E223.visualSharp", {"position": v(10.07, -1.16) * mm});
            skArc(sketch, "E223.filletArc", {"start": v(11.1, -0.69) * mm, "mid": v(10.97, -0.97) * mm, "end": v(11.2, -1.17) * mm});
            skPoint(sketch, "E224.visualSharp", {"position": v(-4.5, -7.78) * mm});
            skArc(sketch, "E224.filletArc", {"start": v(-5.04, -8.54) * mm, "mid": v(-5.05, -8.24) * mm, "end": v(-5.34, -8.17) * mm});
            skLineSegment(sketch, "E225", {"start": v(11.88, -25.43) * mm, "end": v(11.54, -25.54) * mm});
            skLineSegment(sketch, "E226", {"start": v(11.54, -25.54) * mm, "end": v(11.78, -25.78) * mm});
            skPoint(sketch, "E227.oppositeSnap0", {"position": v(-27.48, 34.53) * mm});
            skLineSegment(sketch, "E227.bottom", {"start": v(-29.86, 34.78) * mm, "end": v(-27.32, 34.78) * mm});
            skLineSegment(sketch, "E227.top", {"start": v(-30.04, 34.53) * mm, "end": v(-27.48, 34.53) * mm});
            skPoint(sketch, "E228.oppositeSnap0", {"position": v(-18.2, 32.99) * mm});
            skLineSegment(sketch, "E228.bottom", {"start": v(-20.8, 33.09) * mm, "end": v(-18.2, 33.09) * mm});
            skLineSegment(sketch, "E228.top", {"start": v(-20.8, 32.99) * mm, "end": v(-18.2, 32.99) * mm});
            skPoint(sketch, "E229.oppositeSnap0", {"position": v(-18.2, 35.96) * mm});
            skLineSegment(sketch, "E229.bottom", {"start": v(-20.8, 36.06) * mm, "end": v(-18.2, 36.06) * mm});
            skLineSegment(sketch, "E229.top", {"start": v(-20.8, 35.96) * mm, "end": v(-18.2, 35.96) * mm});
            skLineSegment(sketch, "E230.bottom", {"start": v(0.88, 35.93) * mm, "end": v(3.52, 35.93) * mm});
            skLineSegment(sketch, "E230.top", {"start": v(0.88, 35.83) * mm, "end": v(3.52, 35.83) * mm});
            skLineSegment(sketch, "E231.bottom", {"start": v(-8.42, 35.72) * mm, "end": v(-5.68, 35.72) * mm});
            skLineSegment(sketch, "E231.top", {"start": v(-8.47, 35.62) * mm, "end": v(-5.73, 35.62) * mm});
            skLineSegment(sketch, "E232.trimOffspring", {"start": v(0.88, 35.93) * mm, "end": v(0.88, 39.04) * mm});
            skLineSegment(sketch, "E233.trimOffspring", {"start": v(3.52, 35.83) * mm, "end": v(3.52, 34.7) * mm});
            skLineSegment(sketch, "E234.trimOffspring", {"start": v(-8.42, 35.72) * mm, "end": v(-6.54, 39.04) * mm});
            skLineSegment(sketch, "E235.trimOffspring", {"start": v(-5.68, 35.72) * mm, "end": v(-5.03, 36.94) * mm});
            skLineSegment(sketch, "E236.trimOffspring", {"start": v(-20.8, 36.06) * mm, "end": v(-20.8, 38.16) * mm});
            skLineSegment(sketch, "E237.trimOffspring", {"start": v(-18.2, 35.96) * mm, "end": v(-18.2, 35.43) * mm});
            skPoint(sketch, "E229.right.end.orphan", {"position": v(-17.86, 35.96) * mm});
            skLineSegment(sketch, "E238.trimOffspring", {"start": v(-20.8, 33.09) * mm, "end": v(-20.8, 35.96) * mm});
            skLineSegment(sketch, "E239.trimOffspring", {"start": v(-18.2, 32.99) * mm, "end": v(-18.2, 32.46) * mm});
            skPoint(sketch, "E228.right.end.orphan", {"position": v(-17.61, 32.99) * mm});
            skLineSegment(sketch, "E240.trimOffspring", {"start": v(-29.86, 34.78) * mm, "end": v(-28.26, 37.05) * mm});
            skLineSegment(sketch, "E241.trimOffspring", {"start": v(-27.32, 34.78) * mm, "end": v(-26.72, 35.7) * mm});
            skPoint(sketch, "E242.orphan", {"position": v(-26.87, 34.53) * mm});
            skSolve(sketch);
        }
        {
            var Q0;
            Q0=makeQuery(id+"F0.imprint","IMPRINT",FACE,{"disambiguationData":[TD([[makeQuery(id+"F0.imprint","IMPRINT",EDGE,{"derivedFrom":sQuery(id+"F0.wireOp",EDGE,"E0")}),1.0]])]});
            var Q1;
            Q1=makeQuery(id+"F0.imprint","IMPRINT",FACE,{"disambiguationData":[TD([[makeQuery(id+"F0.imprint","IMPRINT",EDGE,{"derivedFrom":sQuery(id+"F0.wireOp",EDGE,"E40")}),-1.0]])]});
            var Q2;
            {var subQ5=sQuery(id+"F0.wireOp",EDGE,"E89");Q2=makeQuery(id+"F0.imprint","IMPRINT",FACE,{"disambiguationData":[TD([[makeQuery(id+"F0.imprint","IMPRINT",EDGE,{"derivedFrom":subQ5}),1.0]])]});}
            var Q3;
            Q3=makeQuery(id+"F0.imprint","IMPRINT",FACE,{"disambiguationData":[TD([[makeQuery(id+"F0.imprint","IMPRINT",EDGE,{"derivedFrom":sQuery(id+"F0.wireOp",EDGE,"E69")}),-1.0]])]});
            var Q4;
            Q4=makeQuery(id+"F0.imprint","IMPRINT",FACE,{"disambiguationData":[TD([[makeQuery(id+"F0.imprint","IMPRINT",EDGE,{"derivedFrom":sQuery(id+"F0.wireOp",EDGE,"E8")}),-1.0]])]});
            var Q5;
            Q5=makeQuery(id+"F0.imprint","IMPRINT",FACE,{"disambiguationData":[TD([[makeQuery(id+"F0.imprint","IMPRINT",EDGE,{"derivedFrom":sQuery(id+"F0.wireOp",EDGE,"E53")}),1.0]])]});
            var Q6;
            Q6=makeQuery(id+"F0.imprint","IMPRINT",FACE,{"disambiguationData":[TD([[makeQuery(id+"F0.imprint","IMPRINT",EDGE,{"derivedFrom":sQuery(id+"F0.wireOp",EDGE,"E12")}),-1.0]])]});
            var Q7;
            Q7=makeQuery(id+"F0.imprint","IMPRINT",FACE,{"disambiguationData":[TD([[makeQuery(id+"F0.imprint","IMPRINT",EDGE,{"derivedFrom":sQuery(id+"F0.wireOp",EDGE,"E18.MirrorCS")}),-1.0]])]});
            var Q8;
            {var subQ5=sQuery(id+"F0.wireOp",EDGE,"E90");Q8=makeQuery(id+"F0.imprint","IMPRINT",FACE,{"disambiguationData":[TD([[makeQuery(id+"F0.imprint","IMPRINT",EDGE,{"derivedFrom":subQ5}),1.0]])]});}
            extrude(context, id + "F1", {"entities" : qUnion([Q0, Q1, Q2, Q3, Q4, Q5, Q6, Q7, Q8]), "depth" : 1 * mm});
        }
        {
            var Q0;
            Q0=makeQuery(id+"F1.opExtrude","CAP_FACE",FACE,{"disambiguationData":[OSD([sQuery(id+"F0.wireOp",EDGE,"E0"),sQuery(id+"F0.wireOp",EDGE,"E1"),sQuery(id+"F0.wireOp",EDGE,"E2"),sQuery(id+"F0.wireOp",EDGE,"E3"),sQuery(id+"F0.wireOp",EDGE,"E4.0"),sQuery(id+"F0.wireOp",EDGE,"E5.0"),sQuery(id+"F0.wireOp",EDGE,"E6"),sQuery(id+"F0.wireOp",EDGE,"E7"),sQuery(id+"F0.wireOp",EDGE,"E16"),sQuery(id+"F0.wireOp",EDGE,"E17.trimOffspring"),sQuery(id+"F0.wireOp",EDGE,"E21.MirrorCS"),sQuery(id+"F0.wireOp",EDGE,"E24.MirrorCS"),sQuery(id+"F0.wireOp",EDGE,"E25.MirrorCS"),sQuery(id+"F0.wireOp",EDGE,"E26.MirrorCS"),sQuery(id+"F0.wireOp",EDGE,"E28.MirrorCS"),sQuery(id+"F0.wireOp",EDGE,"E31.MirrorCS"),sQuery(id+"F0.wireOp",EDGE,"E32.MirrorCS"),sQuery(id+"F0.wireOp",EDGE,"E33"),sQuery(id+"F0.wireOp",EDGE,"E34"),sQuery(id+"F0.wireOp",EDGE,"E35"),sQuery(id+"F0.wireOp",EDGE,"E36"),sQuery(id+"F0.wireOp",EDGE,"E37"),sQuery(id+"F0.wireOp",EDGE,"E38"),sQuery(id+"F0.wireOp",EDGE,"E39"),sQuery(id+"F0.wireOp",EDGE,"E41"),sQuery(id+"F0.wireOp",EDGE,"E44.trimOffspring"),sQuery(id+"F0.wireOp",EDGE,"E45.trimOffspring"),sQuery(id+"F0.wireOp",EDGE,"E46"),sQuery(id+"F0.wireOp",EDGE,"E47"),sQuery(id+"F0.wireOp",EDGE,"E48"),sQuery(id+"F0.wireOp",EDGE,"E49"),sQuery(id+"F0.wireOp",EDGE,"E50"),sQuery(id+"F0.wireOp",EDGE,"E51"),sQuery(id+"F0.wireOp",EDGE,"E52"),sQuery(id+"F0.wireOp",EDGE,"E58"),sQuery(id+"F0.wireOp",EDGE,"E59"),sQuery(id+"F0.wireOp",EDGE,"E60"),sQuery(id+"F0.wireOp",EDGE,"E61"),sQuery(id+"F0.wireOp",EDGE,"E62"),sQuery(id+"F0.wireOp",EDGE,"E63.trimOffspring"),sQuery(id+"F0.wireOp",EDGE,"E66.filletArc"),sQuery(id+"F0.wireOp",EDGE,"E67.filletArc"),sQuery(id+"F0.wireOp",EDGE,"E68"),sQuery(id+"F0.wireOp",EDGE,"E70"),sQuery(id+"F0.wireOp",EDGE,"E73.trimOffspring"),sQuery(id+"F0.wireOp",EDGE,"E74.trimOffspring"),sQuery(id+"F0.wireOp",EDGE,"E75.trimOffspring"),sQuery(id+"F0.wireOp",EDGE,"E76"),sQuery(id+"F0.wireOp",EDGE,"E77"),sQuery(id+"F0.wireOp",EDGE,"E78"),sQuery(id+"F0.wireOp",EDGE,"E79"),sQuery(id+"F0.wireOp",EDGE,"E80"),sQuery(id+"F0.wireOp",EDGE,"E81"),sQuery(id+"F0.wireOp",EDGE,"E82"),sQuery(id+"F0.wireOp",EDGE,"E83"),sQuery(id+"F0.wireOp",EDGE,"E84"),sQuery(id+"F0.wireOp",EDGE,"E85"),sQuery(id+"F0.wireOp",EDGE,"E84"),sQuery(id+"F0.wireOp",EDGE,"E86.trimOffspring"),sQuery(id+"F0.wireOp",EDGE,"E87.trimOffspring"),sQuery(id+"F0.wireOp",EDGE,"E88.trimOffspring"),sQuery(id+"F0.wireOp",EDGE,"E99"),sQuery(id+"F0.wireOp",EDGE,"E100"),sQuery(id+"F0.wireOp",EDGE,"E101.trimOffspring"),sQuery(id+"F0.wireOp",EDGE,"E102.trimOffspring"),sQuery(id+"F0.wireOp",EDGE,"E103"),sQuery(id+"F0.wireOp",EDGE,"E104"),sQuery(id+"F0.wireOp",EDGE,"E105"),sQuery(id+"F0.wireOp",EDGE,"E106.filletArc"),sQuery(id+"F0.wireOp",EDGE,"E107"),sQuery(id+"F0.wireOp",EDGE,"E108"),sQuery(id+"F0.wireOp",EDGE,"E109"),sQuery(id+"F0.wireOp",EDGE,"E111.trimOffspring"),sQuery(id+"F0.wireOp",EDGE,"E112"),sQuery(id+"F0.wireOp",EDGE,"E114.trimOffspring"),sQuery(id+"F0.wireOp",EDGE,"E115"),sQuery(id+"F0.wireOp",EDGE,"E116"),sQuery(id+"F0.wireOp",EDGE,"E117.0"),sQuery(id+"F0.wireOp",EDGE,"E118.0"),sQuery(id+"F0.wireOp",EDGE,"E119.trimOffspring"),sQuery(id+"F0.wireOp",EDGE,"E120.trimOffspring"),sQuery(id+"F0.wireOp",EDGE,"E121.trimOffspring"),sQuery(id+"F0.wireOp",EDGE,"E122"),sQuery(id+"F0.wireOp",EDGE,"E123"),sQuery(id+"F0.wireOp",EDGE,"E124"),sQuery(id+"F0.wireOp",EDGE,"E125"),sQuery(id+"F0.wireOp",EDGE,"E126"),sQuery(id+"F0.wireOp",EDGE,"E127"),sQuery(id+"F0.wireOp",EDGE,"E128"),sQuery(id+"F0.wireOp",EDGE,"E129"),sQuery(id+"F0.wireOp",EDGE,"E130"),sQuery(id+"F0.wireOp",EDGE,"E131.filletArc"),sQuery(id+"F0.wireOp",EDGE,"E132.filletArc"),sQuery(id+"F0.wireOp",EDGE,"E133.filletArc"),sQuery(id+"F0.wireOp",EDGE,"E134.filletArc"),sQuery(id+"F0.wireOp",EDGE,"E135.filletArc"),sQuery(id+"F0.wireOp",EDGE,"E136"),sQuery(id+"F0.wireOp",EDGE,"E137"),sQuery(id+"F0.wireOp",EDGE,"E138"),sQuery(id+"F0.wireOp",EDGE,"E139"),sQuery(id+"F0.wireOp",EDGE,"E140"),sQuery(id+"F0.wireOp",EDGE,"E141"),sQuery(id+"F0.wireOp",EDGE,"E142"),sQuery(id+"F0.wireOp",EDGE,"E143"),sQuery(id+"F0.wireOp",EDGE,"E144"),sQuery(id+"F0.wireOp",EDGE,"E145"),sQuery(id+"F0.wireOp",EDGE,"E146"),sQuery(id+"F0.wireOp",EDGE,"E147"),sQuery(id+"F0.wireOp",EDGE,"E148"),sQuery(id+"F0.wireOp",EDGE,"E149.filletArc"),sQuery(id+"F0.wireOp",EDGE,"E150.filletArc"),sQuery(id+"F0.wireOp",EDGE,"E151.filletArc"),sQuery(id+"F0.wireOp",EDGE,"E152.filletArc"),sQuery(id+"F0.wireOp",EDGE,"E153.filletArc"),sQuery(id+"F0.wireOp",EDGE,"E154.trimOffspring"),sQuery(id+"F0.wireOp",EDGE,"E155"),sQuery(id+"F0.wireOp",EDGE,"E156"),sQuery(id+"F0.wireOp",EDGE,"E157"),sQuery(id+"F0.wireOp",EDGE,"E158"),sQuery(id+"F0.wireOp",EDGE,"E159"),sQuery(id+"F0.wireOp",EDGE,"E160"),sQuery(id+"F0.wireOp",EDGE,"E161"),sQuery(id+"F0.wireOp",EDGE,"E162"),sQuery(id+"F0.wireOp",EDGE,"E163"),sQuery(id+"F0.wireOp",EDGE,"E164"),sQuery(id+"F0.wireOp",EDGE,"E165"),sQuery(id+"F0.wireOp",EDGE,"E166"),sQuery(id+"F0.wireOp",EDGE,"E167"),sQuery(id+"F0.wireOp",EDGE,"E168"),sQuery(id+"F0.wireOp",EDGE,"E169"),sQuery(id+"F0.wireOp",EDGE,"E170"),sQuery(id+"F0.wireOp",EDGE,"E171"),sQuery(id+"F0.wireOp",EDGE,"E172"),sQuery(id+"F0.wireOp",EDGE,"E173"),sQuery(id+"F0.wireOp",EDGE,"E174"),sQuery(id+"F0.wireOp",EDGE,"E175"),sQuery(id+"F0.wireOp",EDGE,"E176"),sQuery(id+"F0.wireOp",EDGE,"E177"),sQuery(id+"F0.wireOp",EDGE,"E178"),sQuery(id+"F0.wireOp",EDGE,"E179"),sQuery(id+"F0.wireOp",EDGE,"E180"),sQuery(id+"F0.wireOp",EDGE,"E181"),sQuery(id+"F0.wireOp",EDGE,"E182"),sQuery(id+"F0.wireOp",EDGE,"E183"),sQuery(id+"F0.wireOp",EDGE,"E184"),sQuery(id+"F0.wireOp",EDGE,"E185"),sQuery(id+"F0.wireOp",EDGE,"E186"),sQuery(id+"F0.wireOp",EDGE,"E187"),sQuery(id+"F0.wireOp",EDGE,"E188"),sQuery(id+"F0.wireOp",EDGE,"E189"),sQuery(id+"F0.wireOp",EDGE,"E190"),sQuery(id+"F0.wireOp",EDGE,"E191"),sQuery(id+"F0.wireOp",EDGE,"E192"),sQuery(id+"F0.wireOp",EDGE,"E193"),sQuery(id+"F0.wireOp",EDGE,"E194"),sQuery(id+"F0.wireOp",EDGE,"E195"),sQuery(id+"F0.wireOp",EDGE,"E196"),sQuery(id+"F0.wireOp",EDGE,"E197"),sQuery(id+"F0.wireOp",EDGE,"E198"),sQuery(id+"F0.wireOp",EDGE,"E199"),sQuery(id+"F0.wireOp",EDGE,"E200"),sQuery(id+"F0.wireOp",EDGE,"E201"),sQuery(id+"F0.wireOp",EDGE,"E202"),sQuery(id+"F0.wireOp",EDGE,"E203"),sQuery(id+"F0.wireOp",EDGE,"E204"),sQuery(id+"F0.wireOp",EDGE,"E205"),sQuery(id+"F0.wireOp",EDGE,"E206"),sQuery(id+"F0.wireOp",EDGE,"E207"),sQuery(id+"F0.wireOp",EDGE,"E208"),sQuery(id+"F0.wireOp",EDGE,"E209"),sQuery(id+"F0.wireOp",EDGE,"E210"),sQuery(id+"F0.wireOp",EDGE,"E211"),sQuery(id+"F0.wireOp",EDGE,"E212"),sQuery(id+"F0.wireOp",EDGE,"E213"),sQuery(id+"F0.wireOp",EDGE,"E214"),sQuery(id+"F0.wireOp",EDGE,"E215"),sQuery(id+"F0.wireOp",EDGE,"E216"),sQuery(id+"F0.wireOp",EDGE,"E217"),sQuery(id+"F0.wireOp",EDGE,"E218.filletArc"),sQuery(id+"F0.wireOp",EDGE,"E219.filletArc"),sQuery(id+"F0.wireOp",EDGE,"E220.filletArc"),sQuery(id+"F0.wireOp",EDGE,"E221.filletArc"),sQuery(id+"F0.wireOp",EDGE,"E222.trimOffspring"),sQuery(id+"F0.wireOp",EDGE,"E223.filletArc"),sQuery(id+"F0.wireOp",EDGE,"E224.filletArc"),sQuery(id+"F0.wireOp",EDGE,"E225"),sQuery(id+"F0.wireOp",EDGE,"E226")])],"isStart":true});
            var sketch = newSketch(context, id + "F2", { "sketchPlane" : qUnion([Q0])});
            skFitSpline(sketch, "E243.0.0", {"points": [v(34.66, -39.57) * mm, v(34.76, -38.67) * mm, v(34.99, -36.74) * mm, v(36.78, -33.56) * mm, v(39.72, -29.87) * mm, v(41.47, -27.67) * mm]});
            skFitSpline(sketch, "E243.0.1", {"points": [v(41.47, -27.67) * mm, v(39.9, -26.1) * mm, v(37.39, -23.56) * mm, v(36.08, -21.38) * mm, v(36.1, -19.9) * mm, v(40.05, -6.47) * mm, v(41.33, 12.34) * mm, v(34.45, 24.82) * mm, v(24.15, 35.31) * mm, v(14.02, 39.34) * mm, v(5.93, 40.68) * mm, v(1.97, 44.18) * mm, v(0, 45.92) * mm]});
            skFitSpline(sketch, "E243.0.2", {"points": [v(0, 45.92) * mm, v(-1.97, 44.18) * mm, v(-5.93, 40.68) * mm, v(-14.02, 39.34) * mm, v(-24.15, 35.31) * mm, v(-34.45, 24.82) * mm, v(-41.33, 12.34) * mm, v(-40.05, -6.47) * mm, v(-36.1, -19.9) * mm, v(-36.08, -21.38) * mm, v(-37.39, -23.56) * mm, v(-39.9, -26.1) * mm, v(-41.47, -27.67) * mm]});
            skFitSpline(sketch, "E243.0.3", {"points": [v(-41.47, -27.67) * mm, v(-39.72, -29.87) * mm, v(-36.78, -33.56) * mm, v(-34.99, -36.74) * mm, v(-34.76, -38.67) * mm, v(-34.66, -39.57) * mm]});
            skLineSegment(sketch, "E243.0.4", {"start": v(-34.66, -39.57) * mm, "end": v(-24.2, -44.08) * mm});
            skFitSpline(sketch, "E243.0.5", {"points": [v(-24.2, -44.08) * mm, v(-23.1, -43.58) * mm, v(-20.66, -42.5) * mm, v(-15.04, -42.3) * mm, v(-9.2, -43.82) * mm, v(-3.28, -43.98) * mm, v(0, -44.08) * mm]});
            skFitSpline(sketch, "E243.0.6", {"points": [v(0, -44.08) * mm, v(3.28, -43.98) * mm, v(9.2, -43.82) * mm, v(15.04, -42.3) * mm, v(20.66, -42.5) * mm, v(23.1, -43.58) * mm, v(24.2, -44.08) * mm]});
            skLineSegment(sketch, "E243.0.7", {"start": v(24.2, -44.08) * mm, "end": v(34.66, -39.57) * mm});
            skSolve(sketch);
        }
        {
            var Q0;
            Q0 = qSketchRegion(id + "F2", true);
            extrude(context, id + "F3", {"entities" : qUnion([Q0]), "operationType" : NewBodyOperationType.ADD, "depth" : .2 * mm});
        }
    });
